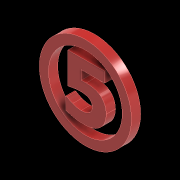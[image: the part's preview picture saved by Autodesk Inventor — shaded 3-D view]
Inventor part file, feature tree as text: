
AUTODESK INVENTOR PART (.ipt)
format: ipt  version: 2020 (Build 240168000, 168)  size: 168,960 bytes
history: native  units: mm
features: other x5, extrude x2, sketch x2
ambient origin geometry x8: Origin, YZ Plane, XZ Plane, XY Plane, X Axis, Y Axis, Z Axis, Center Point
bodies: Body1 (feature_tree)
feature tree (9):
  other  "自動販賣機.ipt"
  extrude  "擠出1"  Depth=10.0mm
  extrude  "擠出2"  Depth=10.0mm TaperAngle=0.0deg
  other  "實體49::自動販賣機.ipt"
  other  "標籤特徵1"
  sketch  "草圖1"
  sketch  "草圖2"
  other  "實體1"
  other  "投影切割邊1"
